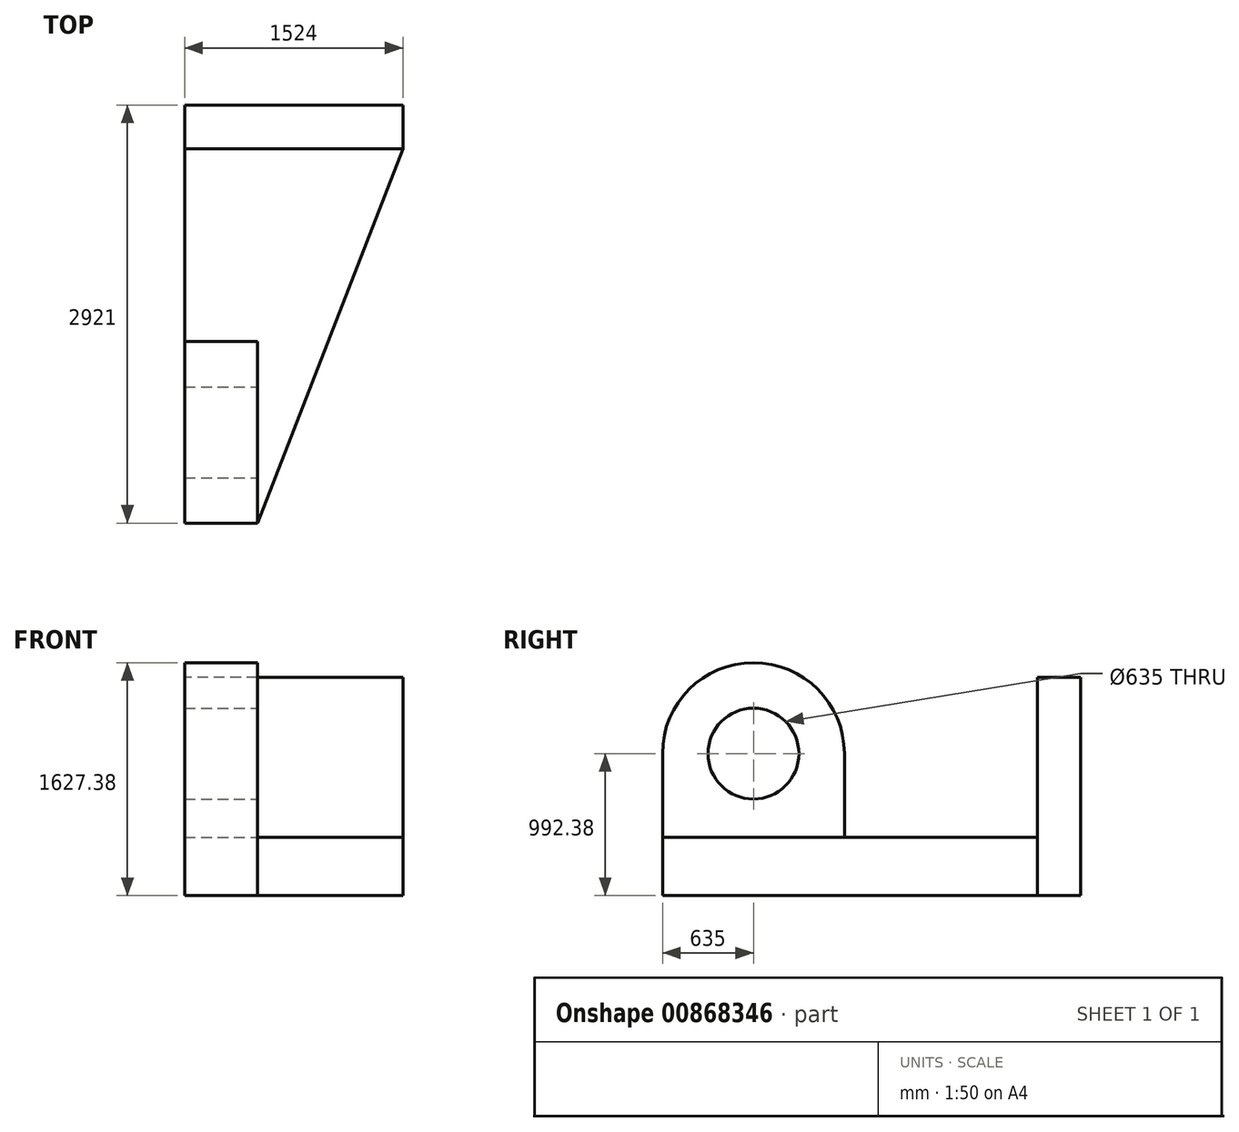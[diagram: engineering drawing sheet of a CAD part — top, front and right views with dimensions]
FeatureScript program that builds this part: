
annotation { "Feature Type Name" : "Feature", "Feature Type Description" : "" }
export const myFeature = defineFeature(function(context is Context, id is Id, definition is map)
    precondition{}
    {
        {
            var Q0;
            Q0=qCreatedBy(makeId("Front.planeOp"),FACE);
            var sketch = newSketch(context, id + "F0", { "sketchPlane" : qUnion([Q0])});
            skLineSegment(sketch, "E0.bottom", {"start": v(0, 0) * mm, "end": v(-1524, 0) * mm});
            skLineSegment(sketch, "E0.top", {"start": v(0, 1524) * mm, "end": v(-1524, 1524) * mm});
            skLineSegment(sketch, "E0.left", {"start": v(0, 0) * mm, "end": v(0, 1524) * mm});
            skLineSegment(sketch, "E0.right", {"start": v(-1524, 0) * mm, "end": v(-1524, 1524) * mm});
            skSolve(sketch);
        }
        {
            var Q0;
            Q0=makeQuery(id+"F0.imprint","IMPRINT",FACE,{"disambiguationData":[TD([[makeQuery(id+"F0.imprint","IMPRINT",EDGE,{"derivedFrom":sQuery(id+"F0.wireOp",EDGE,"E0.bottom")}),-1.0]])]});
            extrude(context, id + "F1", {"entities" : qUnion([Q0]), "depth" : 304.8 * mm, "offsetDistance" : 25.4 * mm});
        }
        {
            var Q0;
            Q0=makeQuery(id+"F1.opExtrude","CAP_FACE",FACE,{"disambiguationData":[OSD([sQuery(id+"F0.wireOp",EDGE,"E0.bottom"),sQuery(id+"F0.wireOp",EDGE,"E0.top"),sQuery(id+"F0.wireOp",EDGE,"E0.left"),sQuery(id+"F0.wireOp",EDGE,"E0.right")])],"isStart":false});
            var sketch = newSketch(context, id + "F2", { "sketchPlane" : qUnion([Q0])});
            skLineSegment(sketch, "E1.bottom", {"start": v(0, 0) * mm, "end": v(-1524, 0) * mm});
            skLineSegment(sketch, "E1.top", {"start": v(0, 408.18) * mm, "end": v(-1524, 408.18) * mm});
            skLineSegment(sketch, "E1.left", {"start": v(0, 0) * mm, "end": v(0, 408.18) * mm});
            skLineSegment(sketch, "E1.right", {"start": v(-1524, 0) * mm, "end": v(-1524, 408.18) * mm});
            skSolve(sketch);
        }
        {
            var Q0;
            Q0=makeQuery(id+"F2.imprint","IMPRINT",FACE,{"disambiguationData":[TD([[makeQuery(id+"F2.imprint","IMPRINT",EDGE,{"derivedFrom":sQuery(id+"F2.wireOp",EDGE,"E1.bottom")}),-1.0]])]});
            extrude(context, id + "F3", {"entities" : qUnion([Q0]), "operationType" : NewBodyOperationType.ADD, "depth" : 2616.2 * mm, "offsetDistance" : 25.4 * mm});
        }
        {
            var Q0;
            Q0=makeQuery(id+"F3.opExtrude","SWEPT_FACE",FACE,{"disambiguationData":[OSD([sQuery(id+"F2.wireOp",EDGE,"E1.top")])]});
            var sketch = newSketch(context, id + "F4", { "sketchPlane" : qUnion([Q0])});
            skLineSegment(sketch, "E2.bottom", {"start": v(-1524, -2921) * mm, "end": v(-1016, -2921) * mm});
            skLineSegment(sketch, "E2.top", {"start": v(-1524, -1651) * mm, "end": v(-1016, -1651) * mm});
            skLineSegment(sketch, "E2.left", {"start": v(-1524, -2921) * mm, "end": v(-1524, -1651) * mm});
            skLineSegment(sketch, "E2.right", {"start": v(-1016, -2921) * mm, "end": v(-1016, -1651) * mm});
            skSolve(sketch);
        }
        {
            var Q0;
            Q0=makeQuery(id+"F4.imprint","IMPRINT",FACE,{"disambiguationData":[TD([[makeQuery(id+"F4.imprint","IMPRINT",EDGE,{"derivedFrom":sQuery(id+"F4.wireOp",EDGE,"E2.bottom")}),-1.0]])]});
            extrude(context, id + "F5", {"entities" : qUnion([Q0]), "operationType" : NewBodyOperationType.ADD, "depth" : 584.2 * mm, "offsetDistance" : 25.4 * mm});
        }
        {
            var Q0;
            Q0=makeQuery(id+"F5.opExtrude","SWEPT_FACE",FACE,{"disambiguationData":[OSD([sQuery(id+"F4.wireOp",EDGE,"E2.right")])]});
            var sketch = newSketch(context, id + "F6", { "sketchPlane" : qUnion([Q0])});
            skCircle(sketch, "E3", {"center": v(-2286, 992.38) * mm, "radius": 635 * mm});
            skSolve(sketch);
        }
        {
            var Q0;
            {var subQ1=sQuery(id+"F4.wireOp",EDGE,"E2.right");var subQ2=makeQuery(id+"F5.opExtrude","CAP_EDGE",EDGE,{"disambiguationData":[OSD([subQ1])],"isStart":false});Q0=makeQuery(id+"F6.imprint","IMPRINT",FACE,{"disambiguationData":[TD([[makeQuery(id+"F6.imprint","IMPRINT",EDGE,{"derivedFrom":subQ2}),1.0]])]});}
            extrude(context, id + "F7", {"entities" : qUnion([Q0]), "operationType" : NewBodyOperationType.ADD, "oppositeDirection" : true, "depth" : 508 * mm, "offsetDistance" : 25.4 * mm});
        }
        {
            var Q0;
            {var subQ0=sQuery(id+"F4.wireOp",EDGE,"E2.right");Q0=makeQuery(id+"F7.boolean.opBoolean","MERGE",FACE,{"derivedFrom":[makeQuery(id+"F5.opExtrude","SWEPT_FACE",FACE,{"disambiguationData":[OSD([subQ0])]}),makeQuery(id+"F7.opExtrude","CAP_FACE",FACE,{"disambiguationData":[OSD([subQ0,sQuery(id+"F6.wireOp",EDGE,"E3")])],"isStart":true})]});}
            var sketch = newSketch(context, id + "F8", { "sketchPlane" : qUnion([Q0])});
            skCircle(sketch, "E4", {"center": v(-2286, 992.38) * mm, "radius": 317.5 * mm});
            skSolve(sketch);
        }
        {
            var Q0;
            Q0=makeQuery(id+"F8.imprint","IMPRINT",FACE,{"disambiguationData":[TD([[makeQuery(id+"F8.imprint","IMPRINT",EDGE,{"derivedFrom":sQuery(id+"F8.wireOp",EDGE,"E4")}),1.0]])]});
            extrude(context, id + "F9", {"entities" : qUnion([Q0]), "operationType" : NewBodyOperationType.REMOVE, "oppositeDirection" : true, "depth" : 508 * mm, "offsetDistance" : 25.4 * mm});
        }
        {
            var Q0;
            Q0=makeQuery(id+"F3.opExtrude","SWEPT_FACE",FACE,{"disambiguationData":[OSD([sQuery(id+"F2.wireOp",EDGE,"E1.top")])]});
            var sketch = newSketch(context, id + "F10", { "sketchPlane" : qUnion([Q0])});
            skLineSegment(sketch, "E5", {"start": v(-1016, -2921) * mm, "end": v(0, -304.8) * mm});
            skSolve(sketch);
        }
        {
            var Q0;
            Q0=makeQuery(id+"F10.imprint","IMPRINT",FACE,{"disambiguationData":[TD([[makeQuery(id+"F10.imprint","IMPRINT",EDGE,{"derivedFrom":sQuery(id+"F10.wireOp",EDGE,"E5")}),-1.0]])]});
            extrude(context, id + "F11", {"entities" : qUnion([Q0]), "operationType" : NewBodyOperationType.REMOVE, "oppositeDirection" : true, "depth" : 579.12 * mm, "offsetDistance" : 25.4 * mm});
        }
    });
